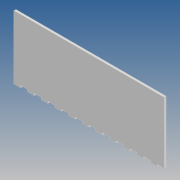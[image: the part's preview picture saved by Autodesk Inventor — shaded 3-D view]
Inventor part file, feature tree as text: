
AUTODESK INVENTOR PART (.ipt)
format: ipt  version: 2020 (Build 240168000, 168)  size: 134,656 bytes
history: native  units: mm
features: extrude x2, sketch x2, other x1, pattern_linear x1
ambient origin geometry x8: Origin, YZ Plane, XZ Plane, XY Plane, X Axis, Y Axis, Z Axis, Center Point
bodies: Body1 (feature_tree)
feature tree (6):
  other  "Твердое тело1"
  extrude  "Выдавливание1"  Depth=10.0mm
  pattern_linear  "Прямоуг.массив1"  Spacing1=3.0mm  [1 undecoded]
  extrude  "Выдавливание2"  Depth=3.0mm TaperAngle=0.0deg
  sketch  "Эскиз1"
  sketch  "Эскиз2"
note: 1 required parameter value undecoded (feature->parameter linkage not recoverable at this tier; creation-order binding heuristic only, values carry confidence <= 0.55)
